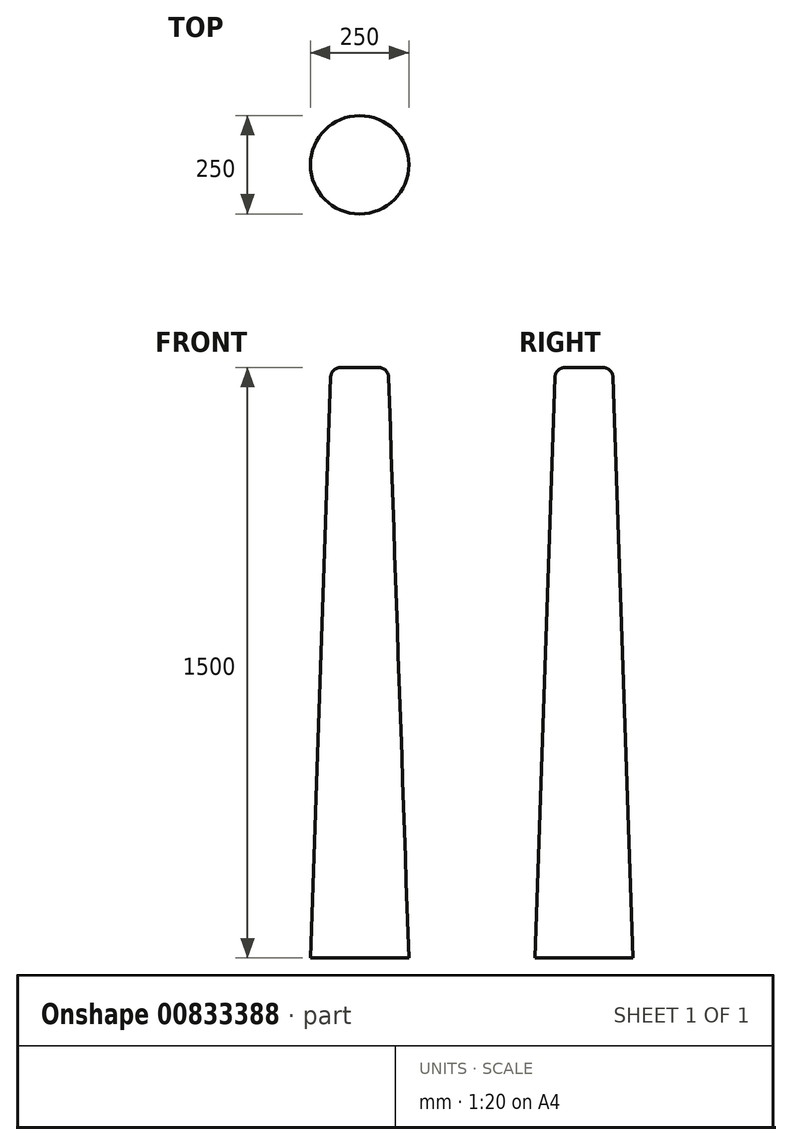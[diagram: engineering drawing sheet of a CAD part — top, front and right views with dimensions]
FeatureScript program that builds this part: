
annotation { "Feature Type Name" : "Feature", "Feature Type Description" : "" }
export const myFeature = defineFeature(function(context is Context, id is Id, definition is map)
    precondition{}
    {
        {
            var Q0;
            Q0=qCreatedBy(makeId("Top.planeOp"),FACE);
            var sketch = newSketch(context, id + "F0", { "sketchPlane" : qUnion([Q0])});
            skCircle(sketch, "E0", {"center": v(0, 0) * mm, "radius": 125 * mm});
            skSolve(sketch);
        }
        {
            var Q0;
            Q0=qSketchRegion(id+"F0",true);
            extrude(context, id + "F1", {"entities" : qUnion([Q0]), "depth" : 1500 * mm, "offsetDistance" : 25 * mm, "hasDraft" : true, "draftAngle" : 2 * degree, "draftPullDirection" : true});
        }
        {
            var Q0;
            Q0=makeQuery(id+"F1.opExtrude","CAP_EDGE",EDGE,{"disambiguationData":[OSD([sQuery(id+"F0.wireOp",EDGE,"E0")])],"isStart":false});
            fillet(context, id + "F2", {"entities" : qUnion([Q0]), "radius" : 25 * mm, "tangentPropagation" : true, "allowEdgeOverflow" : false});
        }
    });
